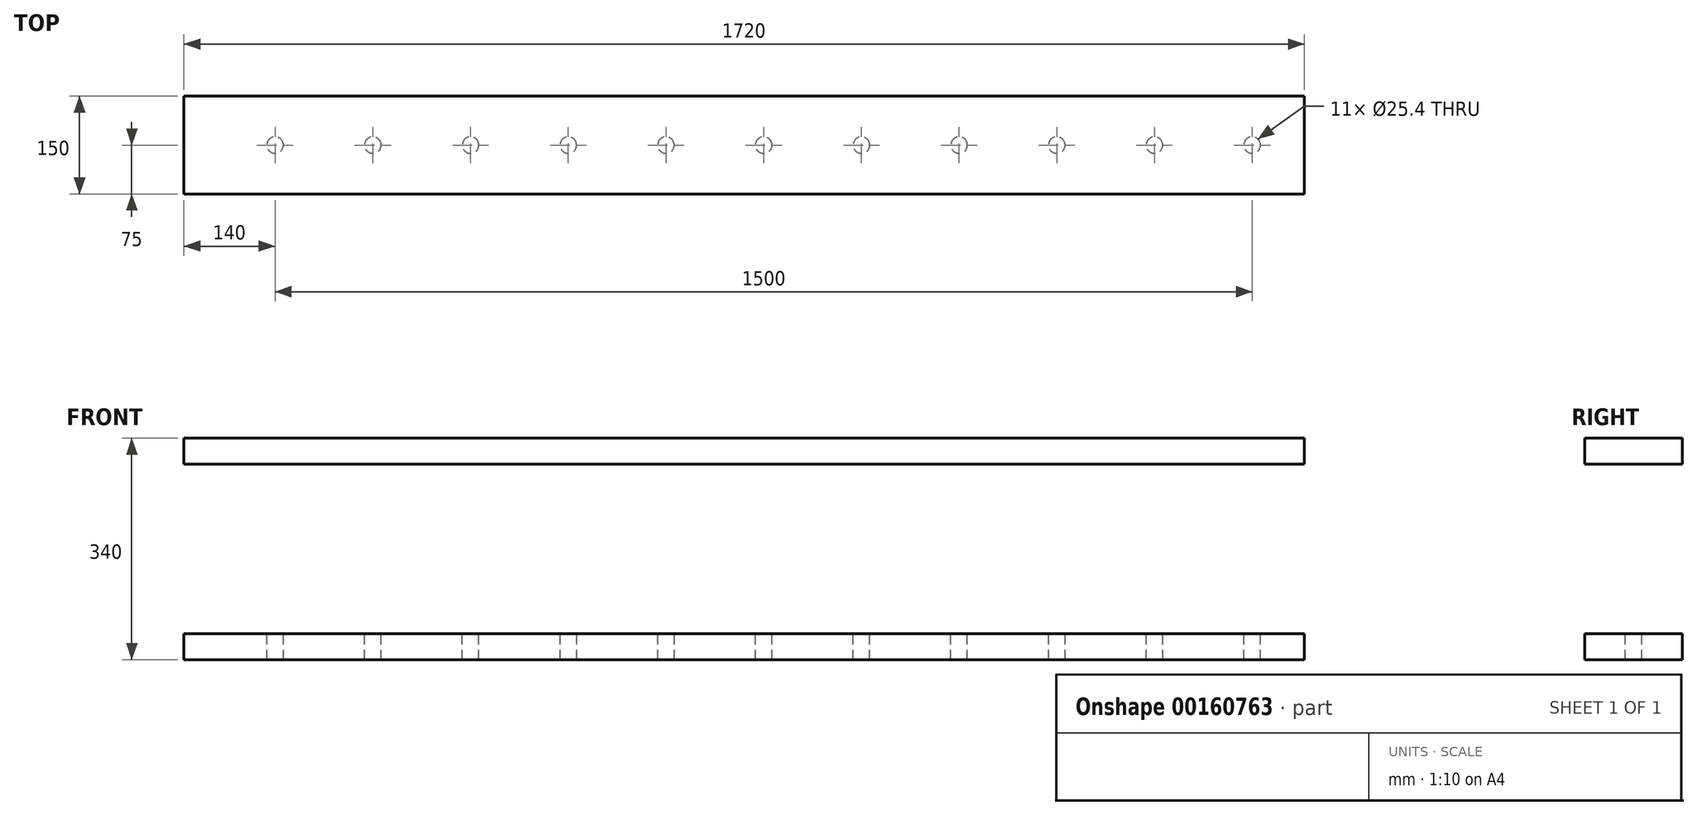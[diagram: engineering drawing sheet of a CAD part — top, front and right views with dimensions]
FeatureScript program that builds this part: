
annotation { "Feature Type Name" : "Feature", "Feature Type Description" : "" }
export const myFeature = defineFeature(function(context is Context, id is Id, definition is map)
    precondition{}
    {
        {
            assignVariable(context, id + "F0", {"name" : "t", "anyValue" : 40 * mm});
        }
        {
            var Q0;
            Q0=qCreatedBy(makeId("Top.planeOp"),FACE);
            var sketch = newSketch(context, id + "F1", { "sketchPlane" : qUnion([Q0])});
            skLineSegment(sketch, "E0.bottom", {"start": v(860, -75) * mm, "end": v(-860, -75) * mm});
            skLineSegment(sketch, "E0.top", {"start": v(860, 75) * mm, "end": v(-860, 75) * mm});
            skLineSegment(sketch, "E0.left", {"start": v(860, -75) * mm, "end": v(860, 75) * mm});
            skLineSegment(sketch, "E0.right", {"start": v(-860, -75) * mm, "end": v(-860, 75) * mm});
            skPoint(sketch, "E0.middle", {"position": v(0, 0) * mm});
            skLineSegment(sketch, "E1", {"start": v(-860, 0) * mm, "end": v(860, 0) * mm, "construction": true});
            skCircle(sketch, "E2", {"center": v(780, 0) * mm, "radius": 12.7 * mm});
            skCircle(sketch, "E3.1.0.0", {"center": v(630, 0) * mm, "radius": 12.7 * mm});
            skCircle(sketch, "E3.2.0.0", {"center": v(480, 0) * mm, "radius": 12.7 * mm});
            skCircle(sketch, "E3.3.0.0", {"center": v(330, 0) * mm, "radius": 12.7 * mm});
            skCircle(sketch, "E3.4.0.0", {"center": v(180, 0) * mm, "radius": 12.7 * mm});
            skCircle(sketch, "E3.5.0.0", {"center": v(30, 0) * mm, "radius": 12.7 * mm});
            skCircle(sketch, "E3.6.0.0", {"center": v(-120, 0) * mm, "radius": 12.7 * mm});
            skCircle(sketch, "E3.7.0.0", {"center": v(-270, 0) * mm, "radius": 12.7 * mm});
            skCircle(sketch, "E3.8.0.0", {"center": v(-420, 0) * mm, "radius": 12.7 * mm});
            skCircle(sketch, "E3.9.0.0", {"center": v(-570, 0) * mm, "radius": 12.7 * mm});
            skLineSegment(sketch, "E3.direction1", {"start": v(780, 0) * mm, "end": v(630, 0) * mm, "construction": true});
            skCircle(sketch, "E4.0.10.0", {"center": v(-720, 0) * mm, "radius": 12.7 * mm});
            skSolve(sketch);
        }
        {
            var Q0;
            Q0 = qSketchRegion(id + "F1", true);
            extrude(context, id + "F2", {"entities" : qUnion([Q0]), "oppositeDirection" : true, "depth" : getVariable(context, 't')});
        }
        {
            var Q0;
            Q0=makeQuery(id+"F1.imprint","IMPRINT",FACE,{"disambiguationData":[TD([[makeQuery(id+"F1.imprint","IMPRINT",EDGE,{"derivedFrom":sQuery(id+"F1.wireOp",EDGE,"E3.9.0.0")}),1.0]])]});
            var Q1;
            Q1=makeQuery(id+"F1.imprint","IMPRINT",FACE,{"disambiguationData":[TD([[makeQuery(id+"F1.imprint","IMPRINT",EDGE,{"derivedFrom":sQuery(id+"F1.wireOp",EDGE,"E3.8.0.0")}),1.0]])]});
            var Q2;
            Q2=makeQuery(id+"F1.imprint","IMPRINT",FACE,{"disambiguationData":[TD([[makeQuery(id+"F1.imprint","IMPRINT",EDGE,{"derivedFrom":sQuery(id+"F1.wireOp",EDGE,"E3.7.0.0")}),1.0]])]});
            var Q3;
            Q3=makeQuery(id+"F1.imprint","IMPRINT",FACE,{"disambiguationData":[TD([[makeQuery(id+"F1.imprint","IMPRINT",EDGE,{"derivedFrom":sQuery(id+"F1.wireOp",EDGE,"E3.6.0.0")}),1.0]])]});
            var Q4;
            Q4=makeQuery(id+"F1.imprint","IMPRINT",FACE,{"disambiguationData":[TD([[makeQuery(id+"F1.imprint","IMPRINT",EDGE,{"derivedFrom":sQuery(id+"F1.wireOp",EDGE,"E3.5.0.0")}),1.0]])]});
            var Q5;
            Q5=makeQuery(id+"F1.imprint","IMPRINT",FACE,{"disambiguationData":[TD([[makeQuery(id+"F1.imprint","IMPRINT",EDGE,{"derivedFrom":sQuery(id+"F1.wireOp",EDGE,"E3.4.0.0")}),1.0]])]});
            var Q6;
            Q6=makeQuery(id+"F1.imprint","IMPRINT",FACE,{"disambiguationData":[TD([[makeQuery(id+"F1.imprint","IMPRINT",EDGE,{"derivedFrom":sQuery(id+"F1.wireOp",EDGE,"E4.0.10.0")}),1.0]])]});
            var Q7;
            Q7=makeQuery(id+"F1.imprint","IMPRINT",FACE,{"disambiguationData":[TD([[makeQuery(id+"F1.imprint","IMPRINT",EDGE,{"derivedFrom":sQuery(id+"F1.wireOp",EDGE,"E3.2.0.0")}),1.0]])]});
            var Q8;
            Q8=makeQuery(id+"F1.imprint","IMPRINT",FACE,{"disambiguationData":[TD([[makeQuery(id+"F1.imprint","IMPRINT",EDGE,{"derivedFrom":sQuery(id+"F1.wireOp",EDGE,"E3.3.0.0")}),1.0]])]});
            var Q9;
            Q9=makeQuery(id+"F1.imprint","IMPRINT",FACE,{"disambiguationData":[TD([[makeQuery(id+"F1.imprint","IMPRINT",EDGE,{"derivedFrom":sQuery(id+"F1.wireOp",EDGE,"E3.1.0.0")}),1.0]])]});
            var Q10;
            Q10=makeQuery(id+"F1.imprint","IMPRINT",FACE,{"disambiguationData":[TD([[makeQuery(id+"F1.imprint","IMPRINT",EDGE,{"derivedFrom":sQuery(id+"F1.wireOp",EDGE,"E2")}),1.0]])]});
            var Q11;
            Q11=makeQuery(id+"F1.imprint","IMPRINT",FACE,{"disambiguationData":[TD([[makeQuery(id+"F1.imprint","IMPRINT",EDGE,{"derivedFrom":sQuery(id+"F1.wireOp",EDGE,"E0.bottom")}),-1.0]])]});
            extrude(context, id + "F3", {"entities" : qUnion([Q0, Q1, Q2, Q3, Q4, Q5, Q6, Q7, Q8, Q9, Q10, Q11]), "depth" : 300 * mm, "hasSecondDirection" : true, "secondDirectionOppositeDirection" : false, "secondDirectionDepth" : 300 * mm - getVariable(context, 't')});
        }
    });
